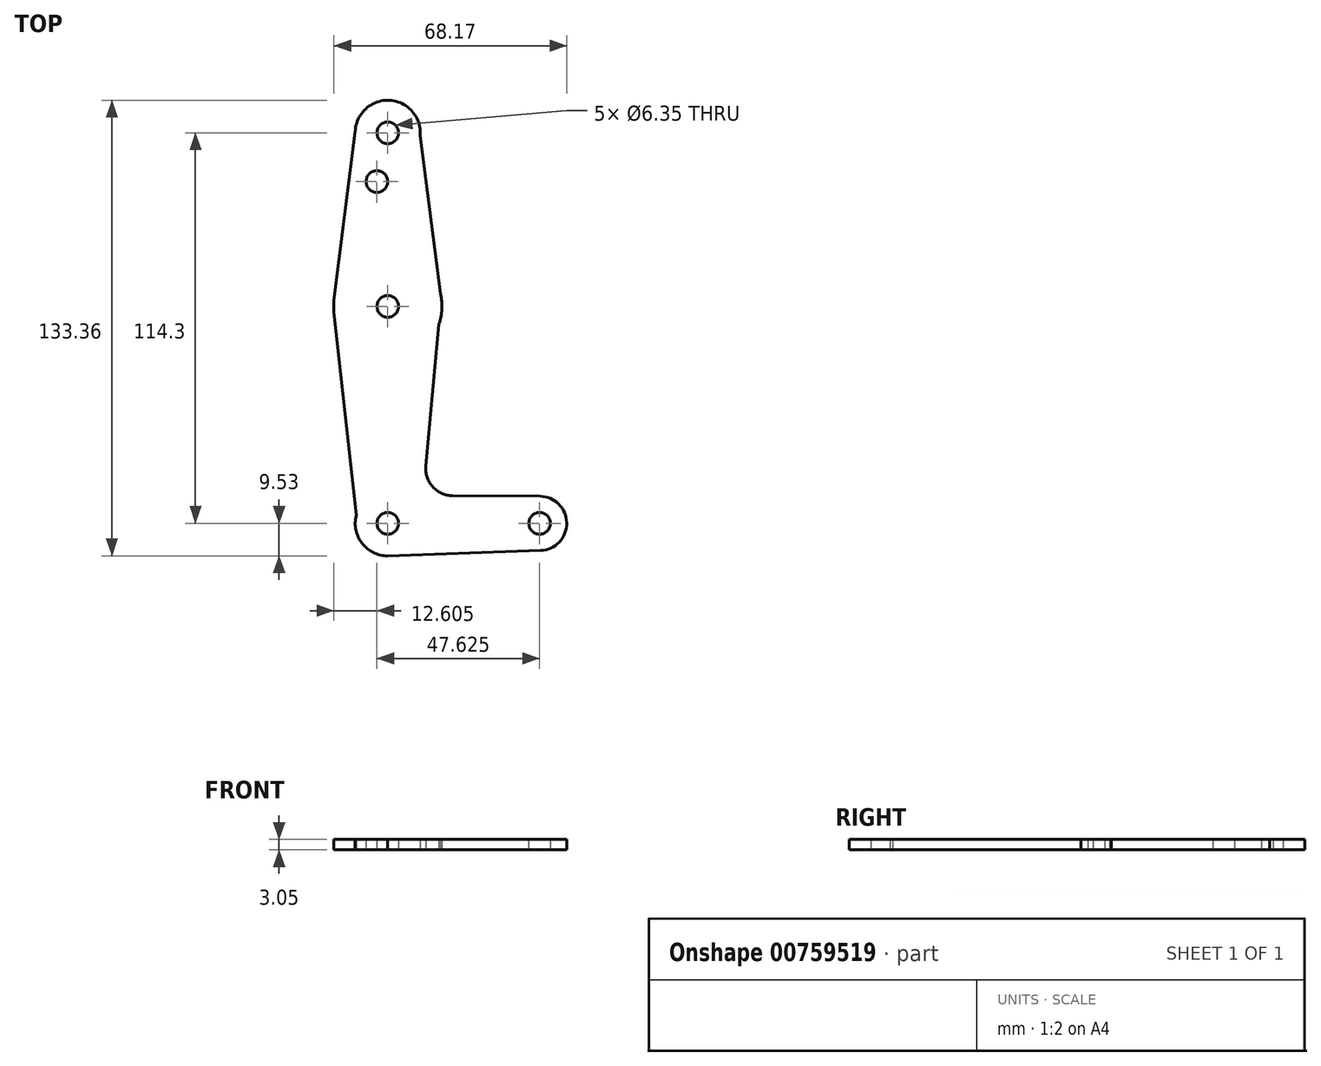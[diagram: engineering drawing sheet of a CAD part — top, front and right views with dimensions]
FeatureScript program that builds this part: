
annotation { "Feature Type Name" : "Feature", "Feature Type Description" : "" }
export const myFeature = defineFeature(function(context is Context, id is Id, definition is map)
    precondition{}
    {
        {
            var Q0;
            Q0=qCreatedBy(makeId("Top.planeOp"),FACE);
            var sketch = newSketch(context, id + "F0", { "sketchPlane" : qUnion([Q0])});
            skLineSegment(sketch, "E0", {"start": v(0, 0) * mm, "end": v(0, 114.3) * mm, "construction": true});
            skLineSegment(sketch, "E1", {"start": v(0, 0) * mm, "end": v(44.45, 0) * mm, "construction": true});
            skCircle(sketch, "E2", {"center": v(0, 0) * mm, "radius": 9.53 * mm});
            skCircle(sketch, "E3", {"center": v(0, 114.3) * mm, "radius": 9.53 * mm});
            skCircle(sketch, "E4", {"center": v(0, 63.5) * mm, "radius": 15.88 * mm});
            skCircle(sketch, "E5", {"center": v(44.45, 0) * mm, "radius": 7.94 * mm});
            skLineSegment(sketch, "E6", {"start": v(9.5, 113.52) * mm, "end": v(15.45, 67.14) * mm});
            skLineSegment(sketch, "E7", {"start": v(-9.52, 114.59) * mm, "end": v(-15.78, 65.24) * mm});
            skLineSegment(sketch, "E8", {"start": v(-15.78, 65.24) * mm, "end": v(-15.78, 61.76) * mm});
            skLineSegment(sketch, "E9", {"start": v(-15.78, 61.76) * mm, "end": v(-9.23, 2.34) * mm});
            skLineSegment(sketch, "E10", {"start": v(15, 58.29) * mm, "end": v(11.13, 16.78) * mm});
            skLineSegment(sketch, "E11", {"start": v(0, -9.53) * mm, "end": v(44.73, -7.93) * mm});
            skLineSegment(sketch, "E12", {"start": v(44.5, 7.94) * mm, "end": v(19, 8.1) * mm});
            skCircle(sketch, "E13", {"center": v(0, 114.3) * mm, "radius": 3.18 * mm});
            skCircle(sketch, "E14", {"center": v(0, 63.5) * mm, "radius": 3.18 * mm});
            skCircle(sketch, "E15", {"center": v(0, 0) * mm, "radius": 3.18 * mm});
            skCircle(sketch, "E16", {"center": v(44.45, 0) * mm, "radius": 3.18 * mm});
            skCircle(sketch, "E17", {"center": v(-3.18, 100.03) * mm, "radius": 3.18 * mm});
            skArc(sketch, "E18.filletArc", {"start": v(11.13, 16.78) * mm, "mid": v(13.15, 10.7) * mm, "end": v(19, 8.1) * mm});
            skSolve(sketch);
        }
        {
            var Q0;
            Q0=makeQuery(id+"F0.imprint","IMPRINT",FACE,{"disambiguationData":[TD([[makeQuery(id+"F0.imprint","IMPRINT",EDGE,{"derivedFrom":sQuery(id+"F0.wireOp",EDGE,"E13")}),-1.0]])]});
            var Q1;
            {var subQ0=sQuery(id+"F0.wireOp",EDGE,"E6");Q1=makeQuery(id+"F0.imprint","IMPRINT",FACE,{"disambiguationData":[TD([[makeQuery(id+"F0.imprint","IMPRINT",EDGE,{"derivedFrom":subQ0}),-1.0]])]});}
            var Q2;
            {var subQ0=sQuery(id+"F0.wireOp",EDGE,"E8");Q2=makeQuery(id+"F0.imprint","IMPRINT",FACE,{"disambiguationData":[TD([[makeQuery(id+"F0.imprint","IMPRINT",EDGE,{"derivedFrom":subQ0}),1.0]])]});}
            var Q3;
            {var subQ0=sQuery(id+"F0.wireOp",EDGE,"E9");Q3=makeQuery(id+"F0.imprint","IMPRINT",FACE,{"disambiguationData":[TD([[makeQuery(id+"F0.imprint","IMPRINT",EDGE,{"derivedFrom":subQ0}),1.0]])]});}
            var Q4;
            Q4=makeQuery(id+"F0.imprint","IMPRINT",FACE,{"disambiguationData":[TD([[makeQuery(id+"F0.imprint","IMPRINT",EDGE,{"derivedFrom":sQuery(id+"F0.wireOp",EDGE,"E15")}),-1.0]])]});
            var Q5;
            Q5=makeQuery(id+"F0.imprint","IMPRINT",FACE,{"disambiguationData":[TD([[makeQuery(id+"F0.imprint","IMPRINT",EDGE,{"derivedFrom":sQuery(id+"F0.wireOp",EDGE,"E16")}),-1.0]])]});
            extrude(context, id + "F1", {"entities" : qUnion([Q0, Q1, Q2, Q3, Q4, Q5]), "depth" : 3.05 * mm, "offsetDistance" : 25.4 * mm});
        }
    });
